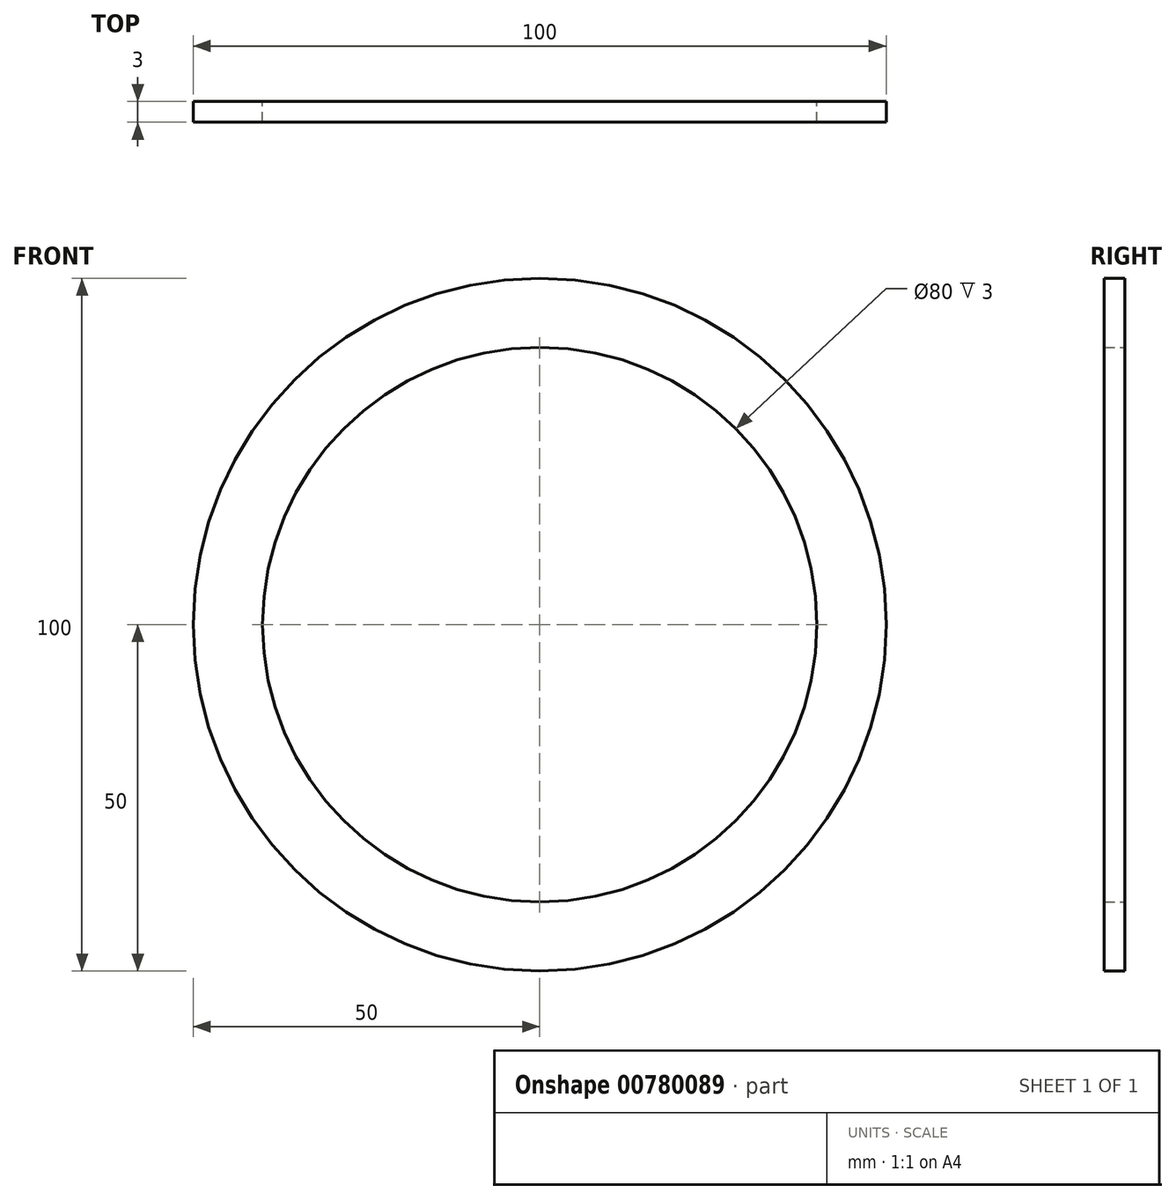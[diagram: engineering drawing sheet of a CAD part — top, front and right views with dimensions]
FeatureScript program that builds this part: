
annotation { "Feature Type Name" : "Feature", "Feature Type Description" : "" }
export const myFeature = defineFeature(function(context is Context, id is Id, definition is map)
    precondition{}
    {
        {
            var Q0;
            Q0=qCreatedBy(makeId("Front.planeOp"),FACE);
            var sketch = newSketch(context, id + "F0", { "sketchPlane" : qUnion([Q0])});
            skCircle(sketch, "E0", {"center": v(0, 0) * mm, "radius": 50 * mm});
            skCircle(sketch, "E1", {"center": v(0, 0) * mm, "radius": 40 * mm});
            skSolve(sketch);
        }
        {
            var Q0;
            Q0=makeQuery(id+"F0.imprint","IMPRINT",FACE,{"disambiguationData":[TD([[makeQuery(id+"F0.imprint","IMPRINT",EDGE,{"derivedFrom":sQuery(id+"F0.wireOp",EDGE,"E0")}),1.0]])]});
            extrude(context, id + "F1", {"entities" : qUnion([Q0]), "depth" : 3 * mm, "offsetDistance" : 25 * mm});
        }
    });
